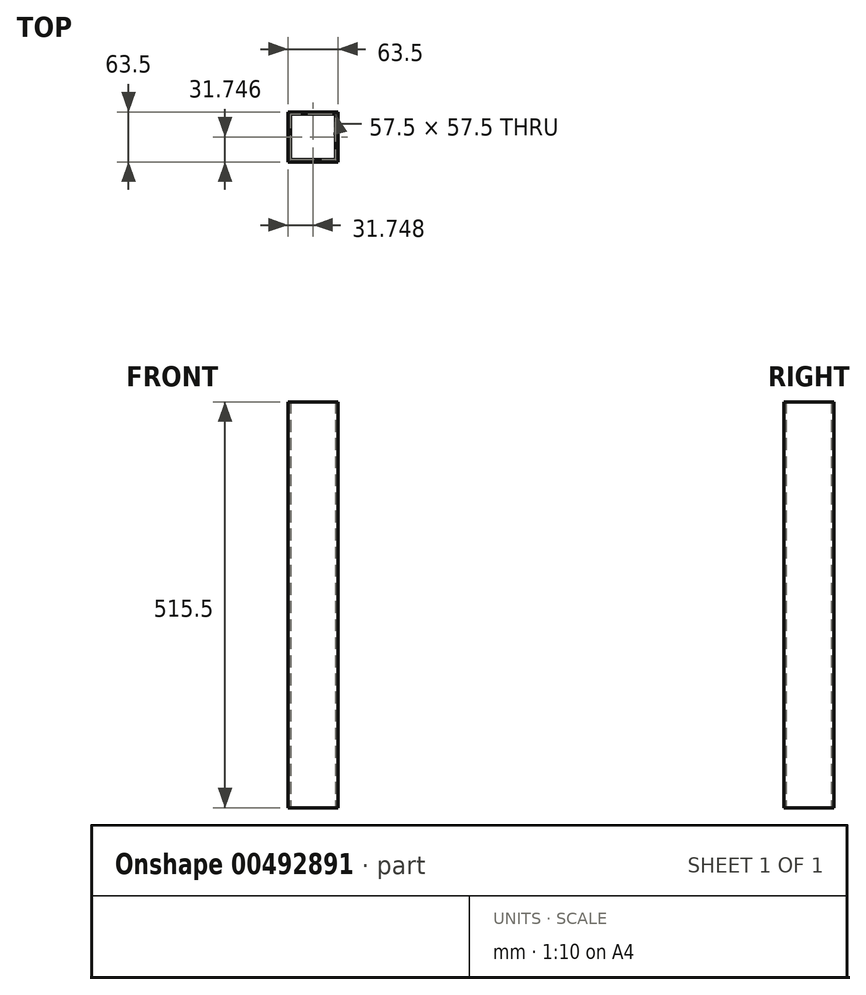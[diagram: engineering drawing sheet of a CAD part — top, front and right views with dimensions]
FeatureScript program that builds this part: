
annotation { "Feature Type Name" : "Feature", "Feature Type Description" : "" }
export const myFeature = defineFeature(function(context is Context, id is Id, definition is map)
    precondition{}
    {
        {
            var Q0;
            Q0=qCreatedBy(makeId("Top.planeOp"),FACE);
            var sketch = newSketch(context, id + "F0", { "sketchPlane" : qUnion([Q0])});
            skLineSegment(sketch, "E0.bottom", {"start": v(-28.85, 19.3) * mm, "end": v(28.65, 19.3) * mm});
            skLineSegment(sketch, "E0.top", {"start": v(-28.85, -38.2) * mm, "end": v(28.65, -38.2) * mm});
            skLineSegment(sketch, "E0.left", {"start": v(-28.85, 19.3) * mm, "end": v(-28.85, -38.2) * mm});
            skLineSegment(sketch, "E0.right", {"start": v(28.65, 19.3) * mm, "end": v(28.65, -38.2) * mm});
            skLineSegment(sketch, "E1.bottom", {"start": v(-31.85, 22.3) * mm, "end": v(31.65, 22.3) * mm});
            skLineSegment(sketch, "E1.top", {"start": v(-31.85, -41.2) * mm, "end": v(31.65, -41.2) * mm});
            skLineSegment(sketch, "E1.left", {"start": v(-31.85, 22.3) * mm, "end": v(-31.85, -41.2) * mm});
            skLineSegment(sketch, "E1.right", {"start": v(31.65, 22.3) * mm, "end": v(31.65, -41.2) * mm});
            skSolve(sketch);
        }
        {
            var Q0;
            Q0 = qSketchRegion(id + "F0", true);
            extrude(context, id + "F1", {"entities" : qUnion([Q0]), "offsetDistance" : 25 * mm, "depth" : 515.5 * mm});
        }
    });
